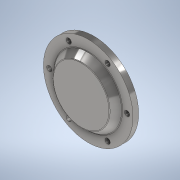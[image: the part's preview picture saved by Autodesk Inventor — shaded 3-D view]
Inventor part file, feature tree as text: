
AUTODESK INVENTOR PART (.ipt)
format: ipt  version: 2020 (Build 240168000, 168)  size: 183,808 bytes
history: native  units: mm
features: sketch x5, reference x4, extrude x3, projected_geometry x3, other x3, plane x2, loft x1, fillet x1
ambient origin geometry x8: Origin, YZ Plane, XZ Plane, XY Plane, X Axis, Y Axis, Z Axis, Center Point
bodies: 实体1 (feature_tree)
feature tree (22):
  plane  "工作平面1"
  extrude  "拉伸1"  Depth=11.0mm
  extrude  "拉伸2"  Depth=12.0mm TaperAngle=0.0deg
  sketch  "草图3"  dims[d8=10.0mm d9=10.5mm d10=0.0mm]
  plane  "工作平面2"
  loft  "放样1"
  extrude  "拉伸3"  Depth=15.0mm
  fillet  "圆角1"  [1 undecoded]
  sketch  "草图1"  dims[d0=165.0mm d1=11.0mm]
  reference  "参考1"
  reference  "参考2"
  reference  "参考3"
  sketch  "草图2"  dims[d2=60.0mm d4=360.0deg d6=12.0mm d7=0.0mm]
  reference  "参考4"
  projected_geometry  "投影回路1"
  sketch  "草图4"  dims[d11=2.0mm d12=15.0mm d13=0.0mm d14=90.0deg]
  projected_geometry  "投影回路2"
  sketch  "草图5"  dims[d15=0.0mm d16=90.0deg d17=5.0mm d18=0.0mm d19=2.0mm]
  projected_geometry  "投影回路3"
  other  "<userpath>\Desktop\ME_course_project\课设试试\shaft_try_1.iam"
  other  "shaft_try_1.iam"
  other  "xia(1):1"
note: 1 required parameter value undecoded (feature->parameter linkage not recoverable at this tier; creation-order binding heuristic only, values carry confidence <= 0.55)
